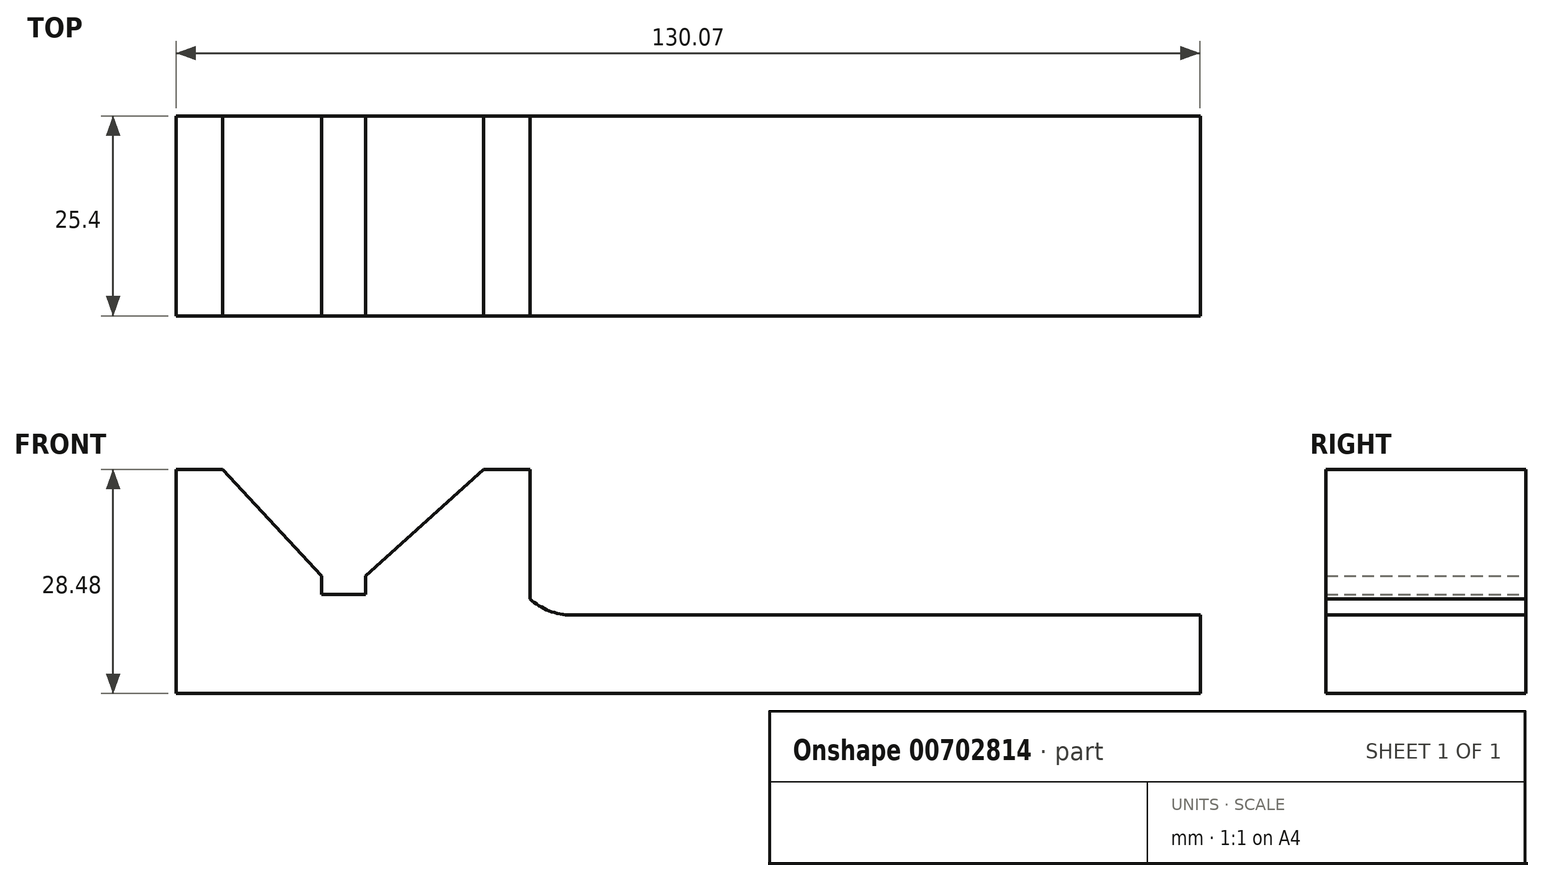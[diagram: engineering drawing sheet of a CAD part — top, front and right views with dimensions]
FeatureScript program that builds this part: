
annotation { "Feature Type Name" : "Feature", "Feature Type Description" : "" }
export const myFeature = defineFeature(function(context is Context, id is Id, definition is map)
    precondition{}
    {
        {
            var Q0;
            Q0=qCreatedBy(makeId("Front.planeOp"),FACE);
            var sketch = newSketch(context, id + "F0", { "sketchPlane" : qUnion([Q0])});
            skLineSegment(sketch, "E0", {"start": v(67.38, -47.27) * mm, "end": v(-62.69, -47.27) * mm});
            skLineSegment(sketch, "E1", {"start": v(-62.69, -47.27) * mm, "end": v(-62.69, -18.8) * mm});
            skLineSegment(sketch, "E2", {"start": v(-62.69, -18.8) * mm, "end": v(-56.81, -18.8) * mm});
            skLineSegment(sketch, "E3", {"start": v(-56.81, -18.8) * mm, "end": v(-44.19, -32.3) * mm});
            skLineSegment(sketch, "E4", {"start": v(-44.19, -32.3) * mm, "end": v(-44.19, -34.65) * mm});
            skLineSegment(sketch, "E5", {"start": v(-44.19, -34.65) * mm, "end": v(-38.61, -34.65) * mm});
            skLineSegment(sketch, "E6", {"start": v(-38.61, -34.65) * mm, "end": v(-38.61, -32.3) * mm});
            skLineSegment(sketch, "E7", {"start": v(-38.61, -32.3) * mm, "end": v(-23.64, -18.8) * mm});
            skLineSegment(sketch, "E8", {"start": v(-23.64, -18.8) * mm, "end": v(-17.76, -18.8) * mm});
            skLineSegment(sketch, "E9", {"start": v(-17.76, -18.8) * mm, "end": v(-17.76, -35.23) * mm});
            skLineSegment(sketch, "E10", {"start": v(67.38, -47.27) * mm, "end": v(67.38, -37.29) * mm});
            skLineSegment(sketch, "E11", {"start": v(67.38, -37.29) * mm, "end": v(-12.48, -37.29) * mm});
            skArc(sketch, "E12", {"start": v(-17.76, -35.23) * mm, "mid": v(-15.31, -36.76) * mm, "end": v(-12.48, -37.29) * mm});
            skSolve(sketch);
        }
        {
            var Q0;
            Q0 = qSketchRegion(id + "F0", true);
            extrude(context, id + "F1", {"entities" : qUnion([Q0]), "depth" : 25.4 * mm, "offsetDistance" : 25.4 * mm});
        }
    });
